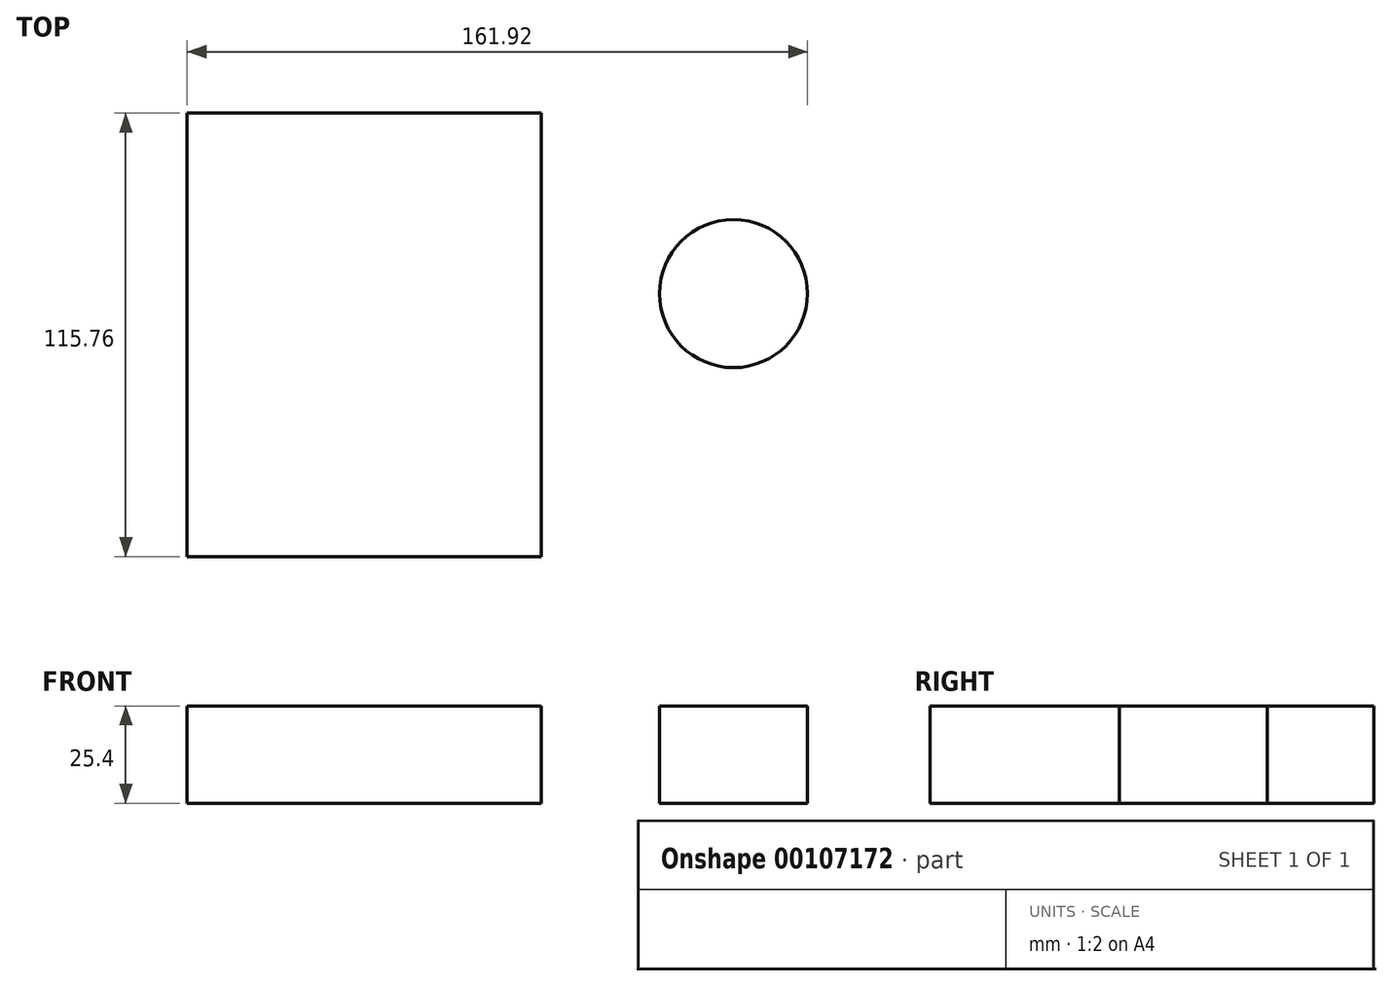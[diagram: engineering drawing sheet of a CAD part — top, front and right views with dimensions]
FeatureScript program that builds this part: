
annotation { "Feature Type Name" : "Feature", "Feature Type Description" : "" }
export const myFeature = defineFeature(function(context is Context, id is Id, definition is map)
    precondition{}
    {
        {
            var Q0;
            Q0=qCreatedBy(makeId("Top.planeOp"),FACE);
            var sketch = newSketch(context, id + "F0", { "sketchPlane" : qUnion([Q0])});
            skLineSegment(sketch, "E0.bottom", {"start": v(86.8, 60.4) * mm, "end": v(-5.63, 60.4) * mm});
            skLineSegment(sketch, "E0.top", {"start": v(86.8, 176.15) * mm, "end": v(-5.63, 176.15) * mm});
            skLineSegment(sketch, "E0.left", {"start": v(86.8, 60.4) * mm, "end": v(86.8, 176.15) * mm});
            skLineSegment(sketch, "E0.right", {"start": v(-5.63, 60.4) * mm, "end": v(-5.63, 176.15) * mm});
            skPoint(sketch, "E0.middle", {"position": v(40.59, 118.27) * mm});
            skSolve(sketch);
        }
        {
            var Q0;
            Q0=makeQuery(id+"F0.imprint","IMPRINT",FACE,{"disambiguationData":[TD([[makeQuery(id+"F0.imprint","IMPRINT",EDGE,{"derivedFrom":sQuery(id+"F0.wireOp",EDGE,"E0.bottom")}),-1.0]])]});
            extrude(context, id + "F1", {"entities" : qUnion([Q0]), "depth" : 25.4 * mm});
        }
        {
            var Q0;
            Q0=qCreatedBy(makeId("Top.planeOp"),FACE);
            var sketch = newSketch(context, id + "F2", { "sketchPlane" : qUnion([Q0])});
            skCircle(sketch, "E1", {"center": v(136.96, 129.04) * mm, "radius": 19.33 * mm});
            skSolve(sketch);
        }
        {
            var Q0;
            Q0 = qSketchRegion(id + "F2", true);
            extrude(context, id + "F3", {"entities" : qUnion([Q0]), "depth" : 25.4 * mm});
        }
    });
